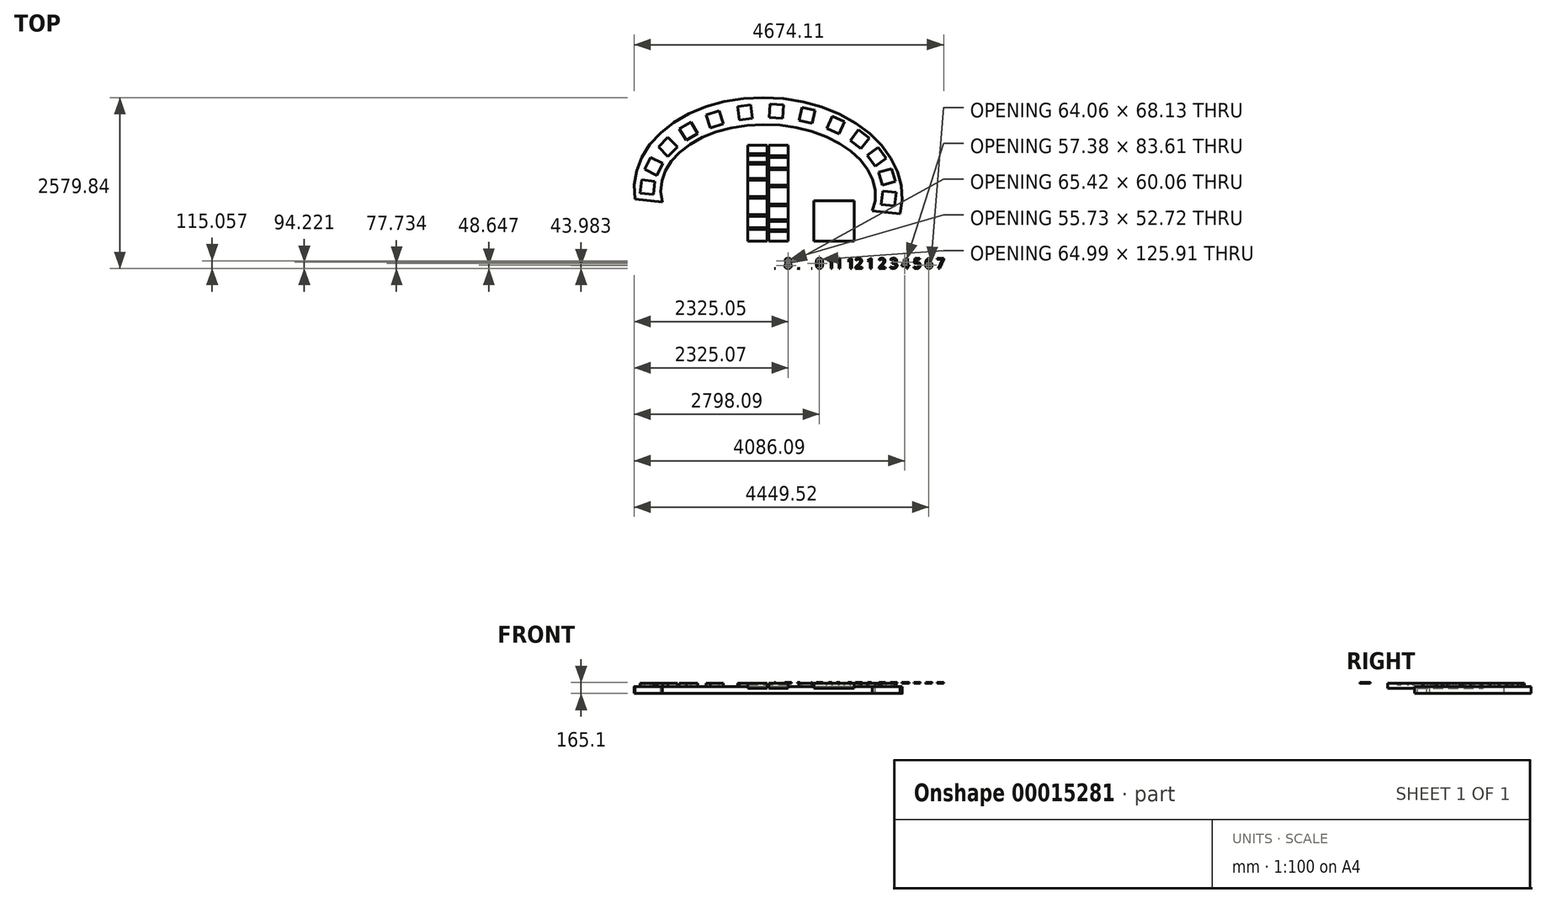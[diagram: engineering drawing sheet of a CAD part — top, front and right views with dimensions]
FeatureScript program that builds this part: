
annotation { "Feature Type Name" : "Feature", "Feature Type Description" : "" }
export const myFeature = defineFeature(function(context is Context, id is Id, definition is map)
    precondition{}
    {
        {
            var Q0;
            Q0=qCreatedBy(makeId("Top.planeOp"),FACE);
            var sketch = newSketch(context, id + "F0", { "sketchPlane" : qUnion([Q0])});
            skLineSegment(sketch, "E0", {"start": v(0, 0) * mm, "end": v(1346.2, 0) * mm, "construction": true});
            skLineSegment(sketch, "E1", {"start": v(0, 0) * mm, "end": v(-1346.2, 0) * mm, "construction": true});
            skLineSegment(sketch, "E2", {"start": v(0, 0) * mm, "end": v(0, 1231.9) * mm, "construction": true});
            skLineSegment(sketch, "E3", {"start": v(0, 0) * mm, "end": v(-1794.42, -235.08) * mm, "construction": true});
            skLineSegment(sketch, "E4", {"start": v(-1794.42, -235.08) * mm, "end": v(0, 1231.9) * mm, "construction": true});
            skLineSegment(sketch, "E5", {"start": v(0, 0) * mm, "end": v(-1820.55, 83.2) * mm, "construction": true});
            skLineSegment(sketch, "E6", {"start": v(-1820.55, 83.2) * mm, "end": v(0, 1231.9) * mm, "construction": true});
            skLineSegment(sketch, "E7", {"start": v(0, 0) * mm, "end": v(-1726.54, 397.25) * mm, "construction": true});
            skLineSegment(sketch, "E8", {"start": v(-1726.54, 397.25) * mm, "end": v(0, 1231.9) * mm, "construction": true});
            skLineSegment(sketch, "E9", {"start": v(0, 0) * mm, "end": v(-1513.04, 691.8) * mm, "construction": true});
            skLineSegment(sketch, "E10", {"start": v(-1513.04, 691.8) * mm, "end": v(0, 1231.9) * mm, "construction": true});
            skLineSegment(sketch, "E11", {"start": v(0, 0) * mm, "end": v(-1200.5, 928.47) * mm, "construction": true});
            skLineSegment(sketch, "E12", {"start": v(-1200.5, 928.47) * mm, "end": v(0, 1231.9) * mm, "construction": true});
            skLineSegment(sketch, "E13", {"start": v(-1346.2, 0) * mm, "end": v(-805.17, 1106.74) * mm, "construction": true});
            skLineSegment(sketch, "E14", {"start": v(-805.17, 1106.74) * mm, "end": v(1346.2, 0) * mm, "construction": true});
            skLineSegment(sketch, "E15", {"start": v(-1346.2, 0) * mm, "end": v(-348.76, 1210.44) * mm, "construction": true});
            skLineSegment(sketch, "E16", {"start": v(-348.76, 1210.44) * mm, "end": v(1346.2, 0) * mm, "construction": true});
            skLineSegment(sketch, "E17", {"start": v(-1346.2, 0) * mm, "end": v(124.87, 1230.26) * mm, "construction": true});
            skLineSegment(sketch, "E18", {"start": v(124.87, 1230.26) * mm, "end": v(1346.2, 0) * mm, "construction": true});
            skLineSegment(sketch, "E19", {"start": v(1346.2, 0) * mm, "end": v(589.88, 1167) * mm, "construction": true});
            skLineSegment(sketch, "E20", {"start": v(589.88, 1167) * mm, "end": v(-1346.2, 0) * mm, "construction": true});
            skLineSegment(sketch, "E21", {"start": v(1346.2, 0) * mm, "end": v(1020.46, 1022.52) * mm, "construction": true});
            skLineSegment(sketch, "E22", {"start": v(1020.46, 1022.52) * mm, "end": v(-1346.2, 0) * mm, "construction": true});
            skLineSegment(sketch, "E23", {"start": v(1346.2, 0) * mm, "end": v(1382.14, 805.65) * mm, "construction": true});
            skLineSegment(sketch, "E24", {"start": v(1382.14, 805.65) * mm, "end": v(-1346.2, 0) * mm, "construction": true});
            skLineSegment(sketch, "E25", {"start": v(0, 1231.9) * mm, "end": v(1639.4, 543.68) * mm, "construction": true});
            skLineSegment(sketch, "E26", {"start": v(1639.4, 543.68) * mm, "end": v(0, 0) * mm, "construction": true});
            skLineSegment(sketch, "E27", {"start": v(0, 0) * mm, "end": v(1794.05, 237.83) * mm, "construction": true});
            skLineSegment(sketch, "E28", {"start": v(1794.05, 237.83) * mm, "end": v(0, 1231.9) * mm, "construction": true});
            skLineSegment(sketch, "E29", {"start": v(0, 1231.9) * mm, "end": v(1820.38, -86.92) * mm, "construction": true});
            skLineSegment(sketch, "E30", {"start": v(1820.38, -86.92) * mm, "end": v(0, 0) * mm, "construction": true});
            skLineSegment(sketch, "E31", {"start": v(0, 0) * mm, "end": v(1726.06, -399.31) * mm, "construction": true});
            skLineSegment(sketch, "E32", {"start": v(1726.06, -399.31) * mm, "end": v(0, 1231.9) * mm, "construction": true});
            skPoint(sketch, "E33", {"position": v(-1794.42, -235.08) * mm});
            skPoint(sketch, "E34", {"position": v(-1820.55, 83.2) * mm});
            skPoint(sketch, "E35", {"position": v(-1726.54, 397.25) * mm});
            skPoint(sketch, "E36", {"position": v(-1513.04, 691.8) * mm});
            skPoint(sketch, "E37", {"position": v(-1200.5, 928.47) * mm});
            skPoint(sketch, "E38", {"position": v(-805.17, 1106.74) * mm});
            skPoint(sketch, "E39", {"position": v(-348.76, 1210.44) * mm});
            skPoint(sketch, "E40", {"position": v(124.87, 1230.26) * mm});
            skPoint(sketch, "E41", {"position": v(589.88, 1167) * mm});
            skPoint(sketch, "E42", {"position": v(1020.46, 1022.52) * mm});
            skPoint(sketch, "E43", {"position": v(1382.14, 805.65) * mm});
            skPoint(sketch, "E44", {"position": v(1639.4, 543.68) * mm});
            skPoint(sketch, "E45", {"position": v(1794.05, 237.83) * mm});
            skPoint(sketch, "E46", {"position": v(1820.38, -86.92) * mm});
            skPoint(sketch, "E47", {"position": v(0, 0) * mm});
            skPoint(sketch, "E48", {"position": v(0, 1231.9) * mm});
            skPoint(sketch, "E49", {"position": v(0, 717.55) * mm});
            skPoint(sketch, "E50", {"position": v(0, -730.25) * mm});
            skPoint(sketch, "E51", {"position": v(0, -571.5) * mm});
            skPoint(sketch, "E52", {"position": v(0, -419.1) * mm});
            skPoint(sketch, "E53", {"position": v(0, -184.15) * mm});
            skPoint(sketch, "E54", {"position": v(0, 101.6) * mm});
            skPoint(sketch, "E55", {"position": v(0, 361.95) * mm});
            skPoint(sketch, "E56", {"position": v(0, 546.1) * mm});
            skPoint(sketch, "E57", {"position": v(0, 577.85) * mm});
            skPoint(sketch, "E58", {"position": v(0, 444.5) * mm});
            skPoint(sketch, "E59", {"position": v(0, 203.2) * mm});
            skPoint(sketch, "E60", {"position": v(0, -69.85) * mm});
            skPoint(sketch, "E61", {"position": v(0, -342.9) * mm});
            skPoint(sketch, "E62", {"position": v(0, -539.75) * mm});
            skSolve(sketch);
        }
        {
            var Q0;
            Q0=qCreatedBy(makeId("Top.planeOp"),FACE);
            var sketch = newSketch(context, id + "F1", { "sketchPlane" : qUnion([Q0])});
            skPoint(sketch, "E63", {"position": v(-1794.42, -235.08) * mm});
            skPoint(sketch, "E64", {"position": v(-1820.55, 83.2) * mm});
            skPoint(sketch, "E65", {"position": v(-1726.54, 397.25) * mm});
            skPoint(sketch, "E66", {"position": v(-1513.04, 691.8) * mm});
            skPoint(sketch, "E67", {"position": v(-1200.5, 928.47) * mm});
            skPoint(sketch, "E68", {"position": v(-805.17, 1106.74) * mm});
            skPoint(sketch, "E69", {"position": v(-348.76, 1210.44) * mm});
            skPoint(sketch, "E70", {"position": v(0, 1231.9) * mm});
            skPoint(sketch, "E71", {"position": v(124.87, 1230.26) * mm});
            skPoint(sketch, "E72", {"position": v(589.88, 1167) * mm});
            skPoint(sketch, "E73", {"position": v(1020.46, 1022.52) * mm});
            skPoint(sketch, "E74", {"position": v(1382.14, 805.65) * mm});
            skPoint(sketch, "E75", {"position": v(1639.4, 543.68) * mm});
            skPoint(sketch, "E76", {"position": v(1794.05, 237.83) * mm});
            skPoint(sketch, "E77", {"position": v(1820.38, -86.92) * mm});
            skPoint(sketch, "E78", {"position": v(1726.06, -399.31) * mm});
            skPoint(sketch, "E79", {"position": v(0, 717.55) * mm});
            skPoint(sketch, "E80", {"position": v(0, 546.1) * mm});
            skPoint(sketch, "E81", {"position": v(0, 361.95) * mm});
            skPoint(sketch, "E82", {"position": v(0, 101.6) * mm});
            skPoint(sketch, "E83", {"position": v(0, -184.15) * mm});
            skPoint(sketch, "E84", {"position": v(0, -419.1) * mm});
            skPoint(sketch, "E85", {"position": v(0, -571.5) * mm});
            skPoint(sketch, "E86", {"position": v(0, -730.25) * mm});
            skLineSegment(sketch, "E87", {"start": v(304.8, 717.55) * mm, "end": v(-304.8, 717.55) * mm});
            skLineSegment(sketch, "E88", {"start": v(0, 546.1) * mm, "end": v(304.8, 546.1) * mm, "construction": true});
            skLineSegment(sketch, "E89", {"start": v(0, 361.95) * mm, "end": v(304.8, 361.95) * mm, "construction": true});
            skLineSegment(sketch, "E90", {"start": v(0, 101.6) * mm, "end": v(304.8, 101.6) * mm, "construction": true});
            skLineSegment(sketch, "E91", {"start": v(0, -184.15) * mm, "end": v(304.8, -184.15) * mm, "construction": true});
            skLineSegment(sketch, "E92", {"start": v(0, -419.1) * mm, "end": v(304.8, -419.1) * mm, "construction": true});
            skLineSegment(sketch, "E93", {"start": v(0, -571.5) * mm, "end": v(304.8, -571.5) * mm, "construction": true});
            skLineSegment(sketch, "E94", {"start": v(-304.8, -730.25) * mm, "end": v(304.8, -730.25) * mm});
            skPoint(sketch, "E95", {"position": v(0, -539.75) * mm});
            skPoint(sketch, "E96", {"position": v(0, -342.9) * mm});
            skPoint(sketch, "E97", {"position": v(0, 203.2) * mm});
            skPoint(sketch, "E98", {"position": v(0, 444.5) * mm});
            skPoint(sketch, "E99", {"position": v(0, 577.85) * mm});
            skPoint(sketch, "E100", {"position": v(0, -69.85) * mm});
            skLineSegment(sketch, "E101", {"start": v(0, -539.75) * mm, "end": v(-304.8, -539.75) * mm, "construction": true});
            skLineSegment(sketch, "E102", {"start": v(0, -342.9) * mm, "end": v(-304.8, -342.9) * mm, "construction": true});
            skLineSegment(sketch, "E103", {"start": v(0, -69.85) * mm, "end": v(-304.8, -69.85) * mm, "construction": true});
            skLineSegment(sketch, "E104", {"start": v(0, 203.2) * mm, "end": v(-304.8, 203.2) * mm, "construction": true});
            skLineSegment(sketch, "E105", {"start": v(0, 444.5) * mm, "end": v(-304.8, 444.5) * mm, "construction": true});
            skLineSegment(sketch, "E106", {"start": v(0, 577.85) * mm, "end": v(-304.8, 577.85) * mm, "construction": true});
            skPoint(sketch, "E107", {"position": v(304.8, -730.25) * mm});
            skPoint(sketch, "E108", {"position": v(-304.8, -730.25) * mm});
            skLineSegment(sketch, "E109", {"start": v(304.8, -730.25) * mm, "end": v(304.8, 717.55) * mm});
            skLineSegment(sketch, "E110", {"start": v(-304.8, -730.25) * mm, "end": v(-304.8, 717.55) * mm});
            skLineSegment(sketch, "E111", {"start": v(0, 717.55) * mm, "end": v(0, -730.25) * mm, "construction": true});
            skLineSegment(sketch, "E112", {"start": v(-1794.42, -235.08) * mm, "end": v(-1726.54, 397.25) * mm, "construction": true});
            skLineSegment(sketch, "E113", {"start": v(-1820.55, 83.2) * mm, "end": v(-1513.04, 691.8) * mm, "construction": true});
            skLineSegment(sketch, "E114", {"start": v(-1726.54, 397.25) * mm, "end": v(-1200.5, 928.47) * mm, "construction": true});
            skLineSegment(sketch, "E115", {"start": v(-1513.04, 691.8) * mm, "end": v(-805.17, 1106.74) * mm, "construction": true});
            skLineSegment(sketch, "E116", {"start": v(-1200.5, 928.47) * mm, "end": v(-348.76, 1210.44) * mm, "construction": true});
            skLineSegment(sketch, "E117", {"start": v(-805.17, 1106.74) * mm, "end": v(124.87, 1230.26) * mm, "construction": true});
            skLineSegment(sketch, "E118", {"start": v(-348.76, 1210.44) * mm, "end": v(589.88, 1167) * mm, "construction": true});
            skLineSegment(sketch, "E119", {"start": v(124.87, 1230.26) * mm, "end": v(1020.46, 1022.52) * mm, "construction": true});
            skLineSegment(sketch, "E120", {"start": v(589.88, 1167) * mm, "end": v(1382.14, 805.65) * mm, "construction": true});
            skLineSegment(sketch, "E121", {"start": v(1020.46, 1022.52) * mm, "end": v(1639.4, 543.68) * mm, "construction": true});
            skLineSegment(sketch, "E122", {"start": v(1382.14, 805.65) * mm, "end": v(1794.05, 237.83) * mm, "construction": true});
            skLineSegment(sketch, "E123", {"start": v(1639.4, 543.68) * mm, "end": v(1820.38, -86.92) * mm, "construction": true});
            skLineSegment(sketch, "E124", {"start": v(1794.05, 237.83) * mm, "end": v(1726.06, -399.31) * mm, "construction": true});
            skCircle(sketch, "E125.cCircle", {"center": v(-1820.55, 83.2) * mm, "radius": 101.6 * mm, "construction": true});
            skLineSegment(sketch, "E125.0", {"start": v(-1932.41, -6.97) * mm, "end": v(-1910.73, 195.07) * mm});
            skLineSegment(sketch, "E125.1", {"start": v(-1910.73, 195.07) * mm, "end": v(-1708.69, 173.38) * mm});
            skLineSegment(sketch, "E125.2", {"start": v(-1708.69, 173.38) * mm, "end": v(-1730.37, -28.66) * mm});
            skLineSegment(sketch, "E125.3", {"start": v(-1730.37, -28.66) * mm, "end": v(-1932.41, -6.97) * mm});
            skPoint(sketch, "E125.0.midPoint", {"position": v(-1921.57, 94.05) * mm});
            skCircle(sketch, "E126.cCircle", {"center": v(-1726.54, 397.25) * mm, "radius": 101.6 * mm, "construction": true});
            skLineSegment(sketch, "E126.0", {"start": v(-1681.68, 260.75) * mm, "end": v(-1863.04, 352.39) * mm});
            skLineSegment(sketch, "E126.1", {"start": v(-1863.04, 352.39) * mm, "end": v(-1771.4, 533.75) * mm});
            skLineSegment(sketch, "E126.2", {"start": v(-1771.4, 533.75) * mm, "end": v(-1590.04, 442.11) * mm});
            skLineSegment(sketch, "E126.3", {"start": v(-1590.04, 442.11) * mm, "end": v(-1681.68, 260.75) * mm});
            skPoint(sketch, "E126.0.midPoint", {"position": v(-1772.36, 306.57) * mm});
            skCircle(sketch, "E127.cCircle", {"center": v(-1513.04, 691.8) * mm, "radius": 101.6 * mm, "construction": true});
            skLineSegment(sketch, "E127.0", {"start": v(-1512.34, 548.12) * mm, "end": v(-1656.73, 691.1) * mm});
            skLineSegment(sketch, "E127.1", {"start": v(-1656.73, 691.1) * mm, "end": v(-1513.75, 835.49) * mm});
            skLineSegment(sketch, "E127.2", {"start": v(-1513.75, 835.49) * mm, "end": v(-1369.36, 692.51) * mm});
            skLineSegment(sketch, "E127.3", {"start": v(-1369.36, 692.51) * mm, "end": v(-1512.34, 548.12) * mm});
            skPoint(sketch, "E127.0.midPoint", {"position": v(-1584.53, 619.61) * mm});
            skCircle(sketch, "E128.cCircle", {"center": v(-1200.5, 928.47) * mm, "radius": 101.6 * mm, "construction": true});
            skLineSegment(sketch, "E128.0", {"start": v(-1236.77, 789.44) * mm, "end": v(-1339.53, 964.75) * mm});
            skLineSegment(sketch, "E128.1", {"start": v(-1339.53, 964.75) * mm, "end": v(-1164.22, 1067.5) * mm});
            skLineSegment(sketch, "E128.2", {"start": v(-1164.22, 1067.5) * mm, "end": v(-1061.47, 892.2) * mm});
            skLineSegment(sketch, "E128.3", {"start": v(-1061.47, 892.2) * mm, "end": v(-1236.77, 789.44) * mm});
            skPoint(sketch, "E128.0.midPoint", {"position": v(-1288.15, 877.1) * mm});
            skCircle(sketch, "E129.cCircle", {"center": v(-805.17, 1106.74) * mm, "radius": 101.6 * mm, "construction": true});
            skLineSegment(sketch, "E129.0", {"start": v(-869.7, 978.35) * mm, "end": v(-933.55, 1171.26) * mm});
            skLineSegment(sketch, "E129.1", {"start": v(-933.55, 1171.26) * mm, "end": v(-740.65, 1235.12) * mm});
            skLineSegment(sketch, "E129.2", {"start": v(-740.65, 1235.12) * mm, "end": v(-676.79, 1042.21) * mm});
            skLineSegment(sketch, "E129.3", {"start": v(-676.79, 1042.21) * mm, "end": v(-869.7, 978.35) * mm});
            skPoint(sketch, "E129.0.midPoint", {"position": v(-901.62, 1074.8) * mm});
            skCircle(sketch, "E130.cCircle", {"center": v(-348.76, 1210.44) * mm, "radius": 101.6 * mm, "construction": true});
            skLineSegment(sketch, "E130.0", {"start": v(-436.1, 1096.34) * mm, "end": v(-462.86, 1297.77) * mm});
            skLineSegment(sketch, "E130.1", {"start": v(-462.86, 1297.77) * mm, "end": v(-261.42, 1324.53) * mm});
            skLineSegment(sketch, "E130.2", {"start": v(-261.42, 1324.53) * mm, "end": v(-234.67, 1123.1) * mm});
            skLineSegment(sketch, "E130.3", {"start": v(-234.67, 1123.1) * mm, "end": v(-436.1, 1096.34) * mm});
            skPoint(sketch, "E130.0.midPoint", {"position": v(-449.48, 1197.06) * mm});
            skCircle(sketch, "E131.cCircle", {"center": v(124.87, 1230.26) * mm, "radius": 101.6 * mm, "construction": true});
            skLineSegment(sketch, "E131.0", {"start": v(231.05, 1327.05) * mm, "end": v(221.66, 1124.07) * mm});
            skLineSegment(sketch, "E131.1", {"start": v(221.66, 1124.07) * mm, "end": v(18.68, 1133.46) * mm});
            skLineSegment(sketch, "E131.2", {"start": v(18.68, 1133.46) * mm, "end": v(28.07, 1336.45) * mm});
            skLineSegment(sketch, "E131.3", {"start": v(28.07, 1336.45) * mm, "end": v(231.05, 1327.05) * mm});
            skPoint(sketch, "E131.0.midPoint", {"position": v(226.36, 1225.56) * mm});
            skCircle(sketch, "E132.cCircle", {"center": v(589.88, 1167) * mm, "radius": 101.6 * mm, "construction": true});
            skLineSegment(sketch, "E132.0", {"start": v(665.9, 1045.07) * mm, "end": v(467.95, 1090.99) * mm});
            skLineSegment(sketch, "E132.1", {"start": v(467.95, 1090.99) * mm, "end": v(513.87, 1288.93) * mm});
            skLineSegment(sketch, "E132.2", {"start": v(513.87, 1288.93) * mm, "end": v(711.81, 1243.02) * mm});
            skLineSegment(sketch, "E132.3", {"start": v(711.81, 1243.02) * mm, "end": v(665.9, 1045.07) * mm});
            skPoint(sketch, "E132.0.midPoint", {"position": v(566.93, 1068.03) * mm});
            skCircle(sketch, "E133.cCircle", {"center": v(1020.46, 1022.52) * mm, "radius": 101.6 * mm, "construction": true});
            skLineSegment(sketch, "E133.0", {"start": v(1155.06, 1072.8) * mm, "end": v(1070.73, 887.92) * mm});
            skLineSegment(sketch, "E133.1", {"start": v(1070.73, 887.92) * mm, "end": v(885.85, 972.24) * mm});
            skLineSegment(sketch, "E133.2", {"start": v(885.85, 972.24) * mm, "end": v(970.18, 1157.12) * mm});
            skLineSegment(sketch, "E133.3", {"start": v(970.18, 1157.12) * mm, "end": v(1155.06, 1072.8) * mm});
            skPoint(sketch, "E133.0.midPoint", {"position": v(1112.9, 980.36) * mm});
            skCircle(sketch, "E134.cCircle", {"center": v(1382.14, 805.65) * mm, "radius": 101.6 * mm, "construction": true});
            skLineSegment(sketch, "E134.0", {"start": v(1524.66, 823.84) * mm, "end": v(1400.33, 663.12) * mm});
            skLineSegment(sketch, "E134.1", {"start": v(1400.33, 663.12) * mm, "end": v(1239.6, 787.46) * mm});
            skLineSegment(sketch, "E134.2", {"start": v(1239.6, 787.46) * mm, "end": v(1363.95, 948.18) * mm});
            skLineSegment(sketch, "E134.3", {"start": v(1363.95, 948.18) * mm, "end": v(1524.66, 823.84) * mm});
            skPoint(sketch, "E134.0.midPoint", {"position": v(1462.5, 743.48) * mm});
            skCircle(sketch, "E135.cCircle", {"center": v(1639.4, 543.68) * mm, "radius": 101.6 * mm, "construction": true});
            skLineSegment(sketch, "E135.0", {"start": v(1616.82, 401.78) * mm, "end": v(1497.5, 566.26) * mm});
            skLineSegment(sketch, "E135.1", {"start": v(1497.5, 566.26) * mm, "end": v(1661.98, 685.58) * mm});
            skLineSegment(sketch, "E135.2", {"start": v(1661.98, 685.58) * mm, "end": v(1781.3, 521.1) * mm});
            skLineSegment(sketch, "E135.3", {"start": v(1781.3, 521.1) * mm, "end": v(1616.82, 401.78) * mm});
            skPoint(sketch, "E135.0.midPoint", {"position": v(1557.16, 484.02) * mm});
            skCircle(sketch, "E136.cCircle", {"center": v(1794.05, 237.83) * mm, "radius": 101.6 * mm, "construction": true});
            skLineSegment(sketch, "E136.0", {"start": v(1919.74, 168.2) * mm, "end": v(1724.42, 112.15) * mm});
            skLineSegment(sketch, "E136.1", {"start": v(1724.42, 112.15) * mm, "end": v(1668.37, 307.46) * mm});
            skLineSegment(sketch, "E136.2", {"start": v(1668.37, 307.46) * mm, "end": v(1863.69, 363.52) * mm});
            skLineSegment(sketch, "E136.3", {"start": v(1863.69, 363.52) * mm, "end": v(1919.74, 168.2) * mm});
            skPoint(sketch, "E136.0.midPoint", {"position": v(1822.08, 140.17) * mm});
            skCircle(sketch, "E137.cCircle", {"center": v(1820.38, -86.92) * mm, "radius": 101.6 * mm, "construction": true});
            skLineSegment(sketch, "E137.0", {"start": v(1910.62, -198.73) * mm, "end": v(1708.57, -177.17) * mm});
            skLineSegment(sketch, "E137.1", {"start": v(1708.57, -177.17) * mm, "end": v(1730.13, 24.89) * mm});
            skLineSegment(sketch, "E137.2", {"start": v(1730.13, 24.89) * mm, "end": v(1932.18, 3.33) * mm});
            skLineSegment(sketch, "E137.3", {"start": v(1932.18, 3.33) * mm, "end": v(1910.62, -198.73) * mm});
            skPoint(sketch, "E137.0.midPoint", {"position": v(1809.6, -187.95) * mm});
            skLineSegment(sketch, "E138.rect.bottom", {"start": v(12.7, -730.25) * mm, "end": v(-12.7, -730.25) * mm});
            skLineSegment(sketch, "E138.rect.left", {"start": v(12.7, -730.25) * mm, "end": v(12.7, 717.55) * mm});
            skLineSegment(sketch, "E138.rect.right", {"start": v(-12.7, -730.25) * mm, "end": v(-12.7, 717.55) * mm});
            skPoint(sketch, "E138.rect.middle", {"position": v(0, 0) * mm});
            skLineSegment(sketch, "E139.bottom", {"start": v(304.8, -584.2) * mm, "end": v(12.7, -584.2) * mm});
            skLineSegment(sketch, "E139.top", {"start": v(304.8, -558.8) * mm, "end": v(12.7, -558.8) * mm});
            skLineSegment(sketch, "E139.left", {"start": v(304.8, -584.2) * mm, "end": v(304.8, -558.8) * mm});
            skLineSegment(sketch, "E139.right", {"start": v(12.7, -584.2) * mm, "end": v(12.7, -558.8) * mm});
            skLineSegment(sketch, "E140.bottom", {"start": v(304.8, -431.8) * mm, "end": v(12.7, -431.8) * mm});
            skLineSegment(sketch, "E140.top", {"start": v(304.8, -406.4) * mm, "end": v(12.7, -406.4) * mm});
            skLineSegment(sketch, "E140.left", {"start": v(304.8, -431.8) * mm, "end": v(304.8, -406.4) * mm});
            skLineSegment(sketch, "E140.right", {"start": v(12.7, -431.8) * mm, "end": v(12.7, -406.4) * mm});
            skLineSegment(sketch, "E141.bottom", {"start": v(304.8, -196.85) * mm, "end": v(12.7, -196.85) * mm});
            skLineSegment(sketch, "E141.top", {"start": v(304.8, -171.45) * mm, "end": v(12.7, -171.45) * mm});
            skLineSegment(sketch, "E141.left", {"start": v(304.8, -196.85) * mm, "end": v(304.8, -171.45) * mm});
            skLineSegment(sketch, "E141.right", {"start": v(12.7, -196.85) * mm, "end": v(12.7, -171.45) * mm});
            skLineSegment(sketch, "E142.bottom", {"start": v(304.8, 88.9) * mm, "end": v(12.7, 88.9) * mm});
            skLineSegment(sketch, "E142.top", {"start": v(304.8, 114.3) * mm, "end": v(12.7, 114.3) * mm});
            skLineSegment(sketch, "E142.left", {"start": v(304.8, 88.9) * mm, "end": v(304.8, 114.3) * mm});
            skLineSegment(sketch, "E142.right", {"start": v(12.7, 88.9) * mm, "end": v(12.7, 114.3) * mm});
            skLineSegment(sketch, "E143.bottom", {"start": v(304.8, 349.25) * mm, "end": v(12.7, 349.25) * mm});
            skLineSegment(sketch, "E143.top", {"start": v(304.8, 374.65) * mm, "end": v(12.7, 374.65) * mm});
            skLineSegment(sketch, "E143.left", {"start": v(304.8, 349.25) * mm, "end": v(304.8, 374.65) * mm});
            skLineSegment(sketch, "E143.right", {"start": v(12.7, 349.25) * mm, "end": v(12.7, 374.65) * mm});
            skLineSegment(sketch, "E144.bottom", {"start": v(304.8, 533.4) * mm, "end": v(12.7, 533.4) * mm});
            skLineSegment(sketch, "E144.top", {"start": v(304.8, 558.8) * mm, "end": v(12.7, 558.8) * mm});
            skLineSegment(sketch, "E144.left", {"start": v(304.8, 533.4) * mm, "end": v(304.8, 558.8) * mm});
            skLineSegment(sketch, "E144.right", {"start": v(12.7, 533.4) * mm, "end": v(12.7, 558.8) * mm});
            skLineSegment(sketch, "E145.bottom", {"start": v(-304.8, 565.15) * mm, "end": v(-12.7, 565.15) * mm});
            skLineSegment(sketch, "E145.top", {"start": v(-304.8, 590.55) * mm, "end": v(-12.7, 590.55) * mm});
            skLineSegment(sketch, "E145.left", {"start": v(-304.8, 565.15) * mm, "end": v(-304.8, 590.55) * mm});
            skLineSegment(sketch, "E145.right", {"start": v(-12.7, 565.15) * mm, "end": v(-12.7, 590.55) * mm});
            skLineSegment(sketch, "E146.bottom", {"start": v(-304.8, 431.8) * mm, "end": v(-12.7, 431.8) * mm});
            skLineSegment(sketch, "E146.top", {"start": v(-304.8, 457.2) * mm, "end": v(-12.7, 457.2) * mm});
            skLineSegment(sketch, "E146.left", {"start": v(-304.8, 431.8) * mm, "end": v(-304.8, 457.2) * mm});
            skLineSegment(sketch, "E146.right", {"start": v(-12.7, 431.8) * mm, "end": v(-12.7, 457.2) * mm});
            skLineSegment(sketch, "E147.bottom", {"start": v(-304.8, 190.5) * mm, "end": v(-12.7, 190.5) * mm});
            skLineSegment(sketch, "E147.top", {"start": v(-304.8, 215.9) * mm, "end": v(-12.7, 215.9) * mm});
            skLineSegment(sketch, "E147.left", {"start": v(-304.8, 190.5) * mm, "end": v(-304.8, 215.9) * mm});
            skLineSegment(sketch, "E147.right", {"start": v(-12.7, 190.5) * mm, "end": v(-12.7, 215.9) * mm});
            skLineSegment(sketch, "E148.bottom", {"start": v(-304.8, -82.55) * mm, "end": v(-12.7, -82.55) * mm});
            skLineSegment(sketch, "E148.top", {"start": v(-304.8, -57.15) * mm, "end": v(-12.7, -57.15) * mm});
            skLineSegment(sketch, "E148.left", {"start": v(-304.8, -82.55) * mm, "end": v(-304.8, -57.15) * mm});
            skLineSegment(sketch, "E148.right", {"start": v(-12.7, -82.55) * mm, "end": v(-12.7, -57.15) * mm});
            skLineSegment(sketch, "E149.bottom", {"start": v(-304.8, -355.6) * mm, "end": v(-12.7, -355.6) * mm});
            skLineSegment(sketch, "E149.top", {"start": v(-304.8, -330.2) * mm, "end": v(-12.7, -330.2) * mm});
            skLineSegment(sketch, "E149.left", {"start": v(-304.8, -355.6) * mm, "end": v(-304.8, -330.2) * mm});
            skLineSegment(sketch, "E149.right", {"start": v(-12.7, -355.6) * mm, "end": v(-12.7, -330.2) * mm});
            skLineSegment(sketch, "E150.bottom", {"start": v(-304.8, -552.45) * mm, "end": v(-12.7, -552.45) * mm});
            skLineSegment(sketch, "E150.top", {"start": v(-304.8, -527.05) * mm, "end": v(-12.7, -527.05) * mm});
            skLineSegment(sketch, "E150.left", {"start": v(-304.8, -552.45) * mm, "end": v(-304.8, -527.05) * mm});
            skLineSegment(sketch, "E150.right", {"start": v(-12.7, -552.45) * mm, "end": v(-12.7, -527.05) * mm});
            skText(sketch, "E151", { "text": "7 8 9 10 11 12 1 2 3 4 5 6 7", "fontName": "OpenSans-Regular.ttf"});
            skLineSegment(sketch, "E152.bottom", {"start": v(65.3, -989.14) * mm, "end": v(211.64, -989.14) * mm});
            skLineSegment(sketch, "E152.top", {"start": v(65.3, -1141.54) * mm, "end": v(211.64, -1141.54) * mm});
            skLineSegment(sketch, "E152.left", {"start": v(65.3, -989.14) * mm, "end": v(65.3, -1141.54) * mm});
            skLineSegment(sketch, "E152.right", {"start": v(211.64, -989.14) * mm, "end": v(211.64, -1141.54) * mm});
            skLineSegment(sketch, "E153.bottom", {"start": v(211.64, -1141.54) * mm, "end": v(385.48, -1141.54) * mm});
            skLineSegment(sketch, "E153.top", {"start": v(211.64, -989.14) * mm, "end": v(385.48, -989.14) * mm});
            skLineSegment(sketch, "E153.left", {"start": v(211.64, -1141.54) * mm, "end": v(211.64, -989.14) * mm});
            skLineSegment(sketch, "E153.right", {"start": v(385.48, -1141.54) * mm, "end": v(385.48, -989.14) * mm});
            skLineSegment(sketch, "E154.bottom", {"start": v(385.48, -1141.54) * mm, "end": v(572.47, -1141.54) * mm});
            skLineSegment(sketch, "E154.top", {"start": v(385.48, -989.14) * mm, "end": v(572.47, -989.14) * mm});
            skLineSegment(sketch, "E154.right", {"start": v(572.47, -1141.54) * mm, "end": v(572.47, -989.14) * mm});
            skLineSegment(sketch, "E155.bottom", {"start": v(572.47, -989.14) * mm, "end": v(870.26, -989.14) * mm});
            skLineSegment(sketch, "E155.top", {"start": v(572.47, -1141.54) * mm, "end": v(870.26, -1141.54) * mm});
            skLineSegment(sketch, "E155.left", {"start": v(572.47, -989.14) * mm, "end": v(572.47, -1141.54) * mm});
            skLineSegment(sketch, "E155.right", {"start": v(870.26, -989.14) * mm, "end": v(870.26, -1141.54) * mm});
            skLineSegment(sketch, "E156", {"start": v(-2863.58, 0) * mm, "end": v(3232.42, -6.97) * mm, "construction": true});
            skLineSegment(sketch, "E157", {"start": v(0, 2273.5) * mm, "end": v(0, -2824.57) * mm, "construction": true});
            skPoint(sketch, "E158", {"position": v(0, 1435.1) * mm});
            skPoint(sketch, "E159", {"position": v(0, 1028.7) * mm});
            skPoint(sketch, "E160", {"position": v(1619.22, -58.91) * mm});
            skPoint(sketch, "E161", {"position": v(2021.73, -113.73) * mm});
            skEllipticalArc(sketch, "E162", {});
            skLineSegment(sketch, "E163", {"start": v(-2012.12, -94.57) * mm, "end": v(-1596.35, -139.2) * mm});
            skLineSegment(sketch, "E164", {"start": v(1574.18, -276.25) * mm, "end": v(1988.6, -320.47) * mm});
            skEllipticalArc(sketch, "E165.trimOffspring", {});
            const initialGuessF1  = {"E151": [0.0653, -1.14154, 1, 0, 0.1524], "E162": [0, 0, 0.9984214700477535, -0.05616554235189876, 2.0249262350496036, 1.4339711488939468, 6.137427259642238, 3.286760696660397], "E165.trimOffspring": [0, 0, 0.9993387333177954, -0.03636063930659239, 1.6202917132659667, 1.0282937856299592, 6.068741439196701, 3.334519765623312]};
            skSetInitialGuess(sketch, initialGuessF1);
            skSolve(sketch);
        }
        {
            var Q0;
            Q0=makeQuery(id+"F1.imprint","IMPRINT",FACE,{"disambiguationData":[TD([[makeQuery(id+"F1.imprint","IMPRINT",EDGE,{"derivedFrom":sQuery(id+"F1.wireOp",EDGE,"E135.0")}),-1.0]])]});
            var Q1;
            Q1=makeQuery(id+"F1.imprint","IMPRINT",FACE,{"disambiguationData":[TD([[makeQuery(id+"F1.imprint","IMPRINT",EDGE,{"derivedFrom":sQuery(id+"F1.wireOp",EDGE,"E134.0")}),-1.0]])]});
            var Q2;
            Q2=makeQuery(id+"F1.imprint","IMPRINT",FACE,{"disambiguationData":[TD([[makeQuery(id+"F1.imprint","IMPRINT",EDGE,{"derivedFrom":sQuery(id+"F1.wireOp",EDGE,"E133.0")}),-1.0]])]});
            var Q3;
            Q3=makeQuery(id+"F1.imprint","IMPRINT",FACE,{"disambiguationData":[TD([[makeQuery(id+"F1.imprint","IMPRINT",EDGE,{"derivedFrom":sQuery(id+"F1.wireOp",EDGE,"E132.0")}),-1.0]])]});
            var Q4;
            Q4=makeQuery(id+"F1.imprint","IMPRINT",FACE,{"disambiguationData":[TD([[makeQuery(id+"F1.imprint","IMPRINT",EDGE,{"derivedFrom":sQuery(id+"F1.wireOp",EDGE,"E131.0")}),-1.0]])]});
            var Q5;
            Q5=makeQuery(id+"F1.imprint","IMPRINT",FACE,{"disambiguationData":[TD([[makeQuery(id+"F1.imprint","IMPRINT",EDGE,{"derivedFrom":sQuery(id+"F1.wireOp",EDGE,"E130.0")}),-1.0]])]});
            var Q6;
            Q6=makeQuery(id+"F1.imprint","IMPRINT",FACE,{"disambiguationData":[TD([[makeQuery(id+"F1.imprint","IMPRINT",EDGE,{"derivedFrom":sQuery(id+"F1.wireOp",EDGE,"E129.0")}),-1.0]])]});
            var Q7;
            Q7=makeQuery(id+"F1.imprint","IMPRINT",FACE,{"disambiguationData":[TD([[makeQuery(id+"F1.imprint","IMPRINT",EDGE,{"derivedFrom":sQuery(id+"F1.wireOp",EDGE,"E128.0")}),-1.0]])]});
            var Q8;
            Q8=makeQuery(id+"F1.imprint","IMPRINT",FACE,{"disambiguationData":[TD([[makeQuery(id+"F1.imprint","IMPRINT",EDGE,{"derivedFrom":sQuery(id+"F1.wireOp",EDGE,"E127.0")}),-1.0]])]});
            var Q9;
            Q9=makeQuery(id+"F1.imprint","IMPRINT",FACE,{"disambiguationData":[TD([[makeQuery(id+"F1.imprint","IMPRINT",EDGE,{"derivedFrom":sQuery(id+"F1.wireOp",EDGE,"E126.0")}),-1.0]])]});
            var Q10;
            Q10=makeQuery(id+"F1.imprint","IMPRINT",FACE,{"disambiguationData":[TD([[makeQuery(id+"F1.imprint","IMPRINT",EDGE,{"derivedFrom":sQuery(id+"F1.wireOp",EDGE,"E125.0")}),-1.0]])]});
            var Q11;
            Q11=makeQuery(id+"F1.imprint","IMPRINT",FACE,{"disambiguationData":[TD([[makeQuery(id+"F1.imprint","IMPRINT",EDGE,{"derivedFrom":sQuery(id+"F1.wireOp",EDGE,"E137.0")}),-1.0]])]});
            var Q12;
            Q12=makeQuery(id+"F1.imprint","IMPRINT",FACE,{"disambiguationData":[TD([[makeQuery(id+"F1.imprint","IMPRINT",EDGE,{"derivedFrom":sQuery(id+"F1.wireOp",EDGE,"E136.0")}),-1.0]])]});
            extrude(context, id + "F2", {"entities" : qUnion([Q0, Q1, Q2, Q3, Q4, Q5, Q6, Q7, Q8, Q9, Q10, Q11, Q12]), "oppositeDirection" : true, "depth" : 50.8 * mm});
        }
        {
            var Q0;
            {var subQ1=sQuery(id+"F1.wireOp",EDGE,"E149.bottom");Q0=makeQuery(id+"F1.imprint","IMPRINT",FACE,{"disambiguationData":[TD([[makeQuery(id+"F1.imprint","IMPRINT",EDGE,{"derivedFrom":subQ1}),-1.0]])]});}
            var Q1;
            {var subQ1=sQuery(id+"F1.wireOp",EDGE,"E148.bottom");Q1=makeQuery(id+"F1.imprint","IMPRINT",FACE,{"disambiguationData":[TD([[makeQuery(id+"F1.imprint","IMPRINT",EDGE,{"derivedFrom":subQ1}),-1.0]])]});}
            var Q2;
            {var subQ0=sQuery(id+"F1.wireOp",EDGE,"E139.bottom");Q2=makeQuery(id+"F1.imprint","IMPRINT",FACE,{"disambiguationData":[TD([[makeQuery(id+"F1.imprint","IMPRINT",EDGE,{"derivedFrom":subQ0}),1.0]])]});}
            var Q3;
            {var subQ0=sQuery(id+"F1.wireOp",EDGE,"E150.bottom");Q3=makeQuery(id+"F1.imprint","IMPRINT",FACE,{"disambiguationData":[TD([[makeQuery(id+"F1.imprint","IMPRINT",EDGE,{"derivedFrom":subQ0}),-1.0]])]});}
            var Q4;
            {var subQ0=sQuery(id+"F1.wireOp",EDGE,"E144.top");Q4=makeQuery(id+"F1.imprint","IMPRINT",FACE,{"disambiguationData":[TD([[makeQuery(id+"F1.imprint","IMPRINT",EDGE,{"derivedFrom":subQ0}),-1.0]])]});}
            var Q5;
            {var subQ0=sQuery(id+"F1.wireOp",EDGE,"E145.top");Q5=makeQuery(id+"F1.imprint","IMPRINT",FACE,{"disambiguationData":[TD([[makeQuery(id+"F1.imprint","IMPRINT",EDGE,{"derivedFrom":subQ0}),1.0]])]});}
            var Q6;
            {var subQ1=sQuery(id+"F1.wireOp",EDGE,"E143.top");Q6=makeQuery(id+"F1.imprint","IMPRINT",FACE,{"disambiguationData":[TD([[makeQuery(id+"F1.imprint","IMPRINT",EDGE,{"derivedFrom":subQ1}),-1.0]])]});}
            var Q7;
            {var subQ1=sQuery(id+"F1.wireOp",EDGE,"E147.bottom");Q7=makeQuery(id+"F1.imprint","IMPRINT",FACE,{"disambiguationData":[TD([[makeQuery(id+"F1.imprint","IMPRINT",EDGE,{"derivedFrom":subQ1}),-1.0]])]});}
            var Q8;
            {var subQ1=sQuery(id+"F1.wireOp",EDGE,"E145.bottom");Q8=makeQuery(id+"F1.imprint","IMPRINT",FACE,{"disambiguationData":[TD([[makeQuery(id+"F1.imprint","IMPRINT",EDGE,{"derivedFrom":subQ1}),-1.0]])]});}
            var Q9;
            {var subQ1=sQuery(id+"F1.wireOp",EDGE,"E139.top");Q9=makeQuery(id+"F1.imprint","IMPRINT",FACE,{"disambiguationData":[TD([[makeQuery(id+"F1.imprint","IMPRINT",EDGE,{"derivedFrom":subQ1}),-1.0]])]});}
            var Q10;
            {var subQ1=sQuery(id+"F1.wireOp",EDGE,"E146.bottom");Q10=makeQuery(id+"F1.imprint","IMPRINT",FACE,{"disambiguationData":[TD([[makeQuery(id+"F1.imprint","IMPRINT",EDGE,{"derivedFrom":subQ1}),-1.0]])]});}
            var Q11;
            {var subQ1=sQuery(id+"F1.wireOp",EDGE,"E141.top");Q11=makeQuery(id+"F1.imprint","IMPRINT",FACE,{"disambiguationData":[TD([[makeQuery(id+"F1.imprint","IMPRINT",EDGE,{"derivedFrom":subQ1}),-1.0]])]});}
            var Q12;
            {var subQ1=sQuery(id+"F1.wireOp",EDGE,"E142.top");Q12=makeQuery(id+"F1.imprint","IMPRINT",FACE,{"disambiguationData":[TD([[makeQuery(id+"F1.imprint","IMPRINT",EDGE,{"derivedFrom":subQ1}),-1.0]])]});}
            var Q13;
            {var subQ1=sQuery(id+"F1.wireOp",EDGE,"E140.top");Q13=makeQuery(id+"F1.imprint","IMPRINT",FACE,{"disambiguationData":[TD([[makeQuery(id+"F1.imprint","IMPRINT",EDGE,{"derivedFrom":subQ1}),-1.0]])]});}
            var Q14;
            Q14=makeQuery(id+"F1.imprint","IMPRINT",FACE,{"disambiguationData":[TD([[makeQuery(id+"F1.imprint","IMPRINT",EDGE,{"derivedFrom":sQuery(id+"F1.wireOp",EDGE,"E150.bottom")}),1.0]])]});
            var Q15;
            {var subQ9=sQuery(id+"F1.wireOp",EDGE,"E138.rect.bottom");Q15=makeQuery(id+"F1.imprint","IMPRINT",FACE,{"disambiguationData":[TD([[makeQuery(id+"F1.imprint","IMPRINT",EDGE,{"derivedFrom":subQ9}),-1.0]])]});}
            var Q16;
            Q16=makeQuery(id+"F1.imprint","IMPRINT",FACE,{"disambiguationData":[TD([[makeQuery(id+"F1.imprint","IMPRINT",EDGE,{"derivedFrom":sQuery(id+"F1.wireOp",EDGE,"E142.bottom")}),-1.0]])]});
            var Q17;
            Q17=makeQuery(id+"F1.imprint","IMPRINT",FACE,{"disambiguationData":[TD([[makeQuery(id+"F1.imprint","IMPRINT",EDGE,{"derivedFrom":sQuery(id+"F1.wireOp",EDGE,"E140.bottom")}),-1.0]])]});
            var Q18;
            Q18=makeQuery(id+"F1.imprint","IMPRINT",FACE,{"disambiguationData":[TD([[makeQuery(id+"F1.imprint","IMPRINT",EDGE,{"derivedFrom":sQuery(id+"F1.wireOp",EDGE,"E139.bottom")}),-1.0]])]});
            var Q19;
            Q19=makeQuery(id+"F1.imprint","IMPRINT",FACE,{"disambiguationData":[TD([[makeQuery(id+"F1.imprint","IMPRINT",EDGE,{"derivedFrom":sQuery(id+"F1.wireOp",EDGE,"E144.bottom")}),-1.0]])]});
            var Q20;
            Q20=makeQuery(id+"F1.imprint","IMPRINT",FACE,{"disambiguationData":[TD([[makeQuery(id+"F1.imprint","IMPRINT",EDGE,{"derivedFrom":sQuery(id+"F1.wireOp",EDGE,"E141.bottom")}),-1.0]])]});
            var Q21;
            Q21=makeQuery(id+"F1.imprint","IMPRINT",FACE,{"disambiguationData":[TD([[makeQuery(id+"F1.imprint","IMPRINT",EDGE,{"derivedFrom":sQuery(id+"F1.wireOp",EDGE,"E149.bottom")}),1.0]])]});
            var Q22;
            Q22=makeQuery(id+"F1.imprint","IMPRINT",FACE,{"disambiguationData":[TD([[makeQuery(id+"F1.imprint","IMPRINT",EDGE,{"derivedFrom":sQuery(id+"F1.wireOp",EDGE,"E147.bottom")}),1.0]])]});
            var Q23;
            Q23=makeQuery(id+"F1.imprint","IMPRINT",FACE,{"disambiguationData":[TD([[makeQuery(id+"F1.imprint","IMPRINT",EDGE,{"derivedFrom":sQuery(id+"F1.wireOp",EDGE,"E148.bottom")}),1.0]])]});
            var Q24;
            Q24=makeQuery(id+"F1.imprint","IMPRINT",FACE,{"disambiguationData":[TD([[makeQuery(id+"F1.imprint","IMPRINT",EDGE,{"derivedFrom":sQuery(id+"F1.wireOp",EDGE,"E146.bottom")}),1.0]])]});
            var Q25;
            Q25=makeQuery(id+"F1.imprint","IMPRINT",FACE,{"disambiguationData":[TD([[makeQuery(id+"F1.imprint","IMPRINT",EDGE,{"derivedFrom":sQuery(id+"F1.wireOp",EDGE,"E145.bottom")}),1.0]])]});
            var Q26;
            Q26=makeQuery(id+"F1.imprint","IMPRINT",FACE,{"disambiguationData":[TD([[makeQuery(id+"F1.imprint","IMPRINT",EDGE,{"derivedFrom":sQuery(id+"F1.wireOp",EDGE,"E143.bottom")}),-1.0]])]});
            extrude(context, id + "F3", {"entities" : qUnion([Q0, Q1, Q2, Q3, Q4, Q5, Q6, Q7, Q8, Q9, Q10, Q11, Q12, Q13, Q14, Q15, Q16, Q17, Q18, Q19, Q20, Q21, Q22, Q23, Q24, Q25, Q26]), "oppositeDirection" : true, "depth" : 76.2 * mm});
        }
        {
            var Q0;
            Q0=makeQuery(id+"F1.imprint","IMPRINT",FACE,{"disambiguationData":[TD([[makeQuery(id+"F1.imprint","IMPRINT",EDGE,{"derivedFrom":sQuery(id+"F1.wireOp",EDGE,"E139.bottom")}),-1.0]])]});
            var Q1;
            Q1=makeQuery(id+"F1.imprint","IMPRINT",FACE,{"disambiguationData":[TD([[makeQuery(id+"F1.imprint","IMPRINT",EDGE,{"derivedFrom":sQuery(id+"F1.wireOp",EDGE,"E150.bottom")}),1.0]])]});
            var Q2;
            Q2=makeQuery(id+"F1.imprint","IMPRINT",FACE,{"disambiguationData":[TD([[makeQuery(id+"F1.imprint","IMPRINT",EDGE,{"derivedFrom":sQuery(id+"F1.wireOp",EDGE,"E140.bottom")}),-1.0]])]});
            var Q3;
            Q3=makeQuery(id+"F1.imprint","IMPRINT",FACE,{"disambiguationData":[TD([[makeQuery(id+"F1.imprint","IMPRINT",EDGE,{"derivedFrom":sQuery(id+"F1.wireOp",EDGE,"E149.bottom")}),1.0]])]});
            var Q4;
            Q4=makeQuery(id+"F1.imprint","IMPRINT",FACE,{"disambiguationData":[TD([[makeQuery(id+"F1.imprint","IMPRINT",EDGE,{"derivedFrom":sQuery(id+"F1.wireOp",EDGE,"E141.bottom")}),-1.0]])]});
            var Q5;
            Q5=makeQuery(id+"F1.imprint","IMPRINT",FACE,{"disambiguationData":[TD([[makeQuery(id+"F1.imprint","IMPRINT",EDGE,{"derivedFrom":sQuery(id+"F1.wireOp",EDGE,"E148.bottom")}),1.0]])]});
            var Q6;
            Q6=makeQuery(id+"F1.imprint","IMPRINT",FACE,{"disambiguationData":[TD([[makeQuery(id+"F1.imprint","IMPRINT",EDGE,{"derivedFrom":sQuery(id+"F1.wireOp",EDGE,"E142.bottom")}),-1.0]])]});
            var Q7;
            Q7=makeQuery(id+"F1.imprint","IMPRINT",FACE,{"disambiguationData":[TD([[makeQuery(id+"F1.imprint","IMPRINT",EDGE,{"derivedFrom":sQuery(id+"F1.wireOp",EDGE,"E147.bottom")}),1.0]])]});
            var Q8;
            Q8=makeQuery(id+"F1.imprint","IMPRINT",FACE,{"disambiguationData":[TD([[makeQuery(id+"F1.imprint","IMPRINT",EDGE,{"derivedFrom":sQuery(id+"F1.wireOp",EDGE,"E143.bottom")}),-1.0]])]});
            var Q9;
            Q9=makeQuery(id+"F1.imprint","IMPRINT",FACE,{"disambiguationData":[TD([[makeQuery(id+"F1.imprint","IMPRINT",EDGE,{"derivedFrom":sQuery(id+"F1.wireOp",EDGE,"E146.bottom")}),1.0]])]});
            var Q10;
            Q10=makeQuery(id+"F1.imprint","IMPRINT",FACE,{"disambiguationData":[TD([[makeQuery(id+"F1.imprint","IMPRINT",EDGE,{"derivedFrom":sQuery(id+"F1.wireOp",EDGE,"E144.bottom")}),-1.0]])]});
            var Q11;
            Q11=makeQuery(id+"F1.imprint","IMPRINT",FACE,{"disambiguationData":[TD([[makeQuery(id+"F1.imprint","IMPRINT",EDGE,{"derivedFrom":sQuery(id+"F1.wireOp",EDGE,"E145.bottom")}),1.0]])]});
            var Q12;
            {var subQ9=sQuery(id+"F1.wireOp",EDGE,"E138.rect.bottom");Q12=makeQuery(id+"F1.imprint","IMPRINT",FACE,{"disambiguationData":[TD([[makeQuery(id+"F1.imprint","IMPRINT",EDGE,{"derivedFrom":subQ9}),-1.0]])]});}
            extrude(context, id + "F4", {"entities" : qUnion([Q0, Q1, Q2, Q3, Q4, Q5, Q6, Q7, Q8, Q9, Q10, Q11, Q12]), "operationType" : NewBodyOperationType.REMOVE, "oppositeDirection" : true, "depth" : 25.4 * mm});
        }
        {
            var Q0;
            {var subQ2=sQuery(id+"F1.wireOp",EDGE,"E151.sketch_text.stroke-0");Q0=makeQuery(id+"F1.imprint","IMPRINT",FACE,{"disambiguationData":[TD([[makeQuery(id+"F1.imprint","IMPRINT",EDGE,{"derivedFrom":subQ2}),-1.0]])]});}
            var Q1;
            {var subQ8=sQuery(id+"F1.wireOp",EDGE,"E151.sketch_text.stroke-8");Q1=makeQuery(id+"F1.imprint","IMPRINT",FACE,{"disambiguationData":[TD([[makeQuery(id+"F1.imprint","IMPRINT",EDGE,{"derivedFrom":subQ8}),-1.0]])]});}
            var Q2;
            {var subQ9=sQuery(id+"F1.wireOp",EDGE,"E151.sketch_text.stroke-40");Q2=makeQuery(id+"F1.imprint","IMPRINT",FACE,{"disambiguationData":[TD([[makeQuery(id+"F1.imprint","IMPRINT",EDGE,{"derivedFrom":subQ9}),-1.0]])]});}
            var Q3;
            {var subQ2=sQuery(id+"F1.wireOp",EDGE,"E151.sketch_text.stroke-65");Q3=makeQuery(id+"F1.imprint","IMPRINT",FACE,{"disambiguationData":[TD([[makeQuery(id+"F1.imprint","IMPRINT",EDGE,{"derivedFrom":subQ2}),-1.0]])]});}
            var Q4;
            {var subQ13=sQuery(id+"F1.wireOp",EDGE,"E151.sketch_text.stroke-73");Q4=makeQuery(id+"F1.imprint","IMPRINT",FACE,{"disambiguationData":[TD([[makeQuery(id+"F1.imprint","IMPRINT",EDGE,{"derivedFrom":subQ13}),-1.0]])]});}
            var Q5;
            Q5=makeQuery(id+"F1.imprint","IMPRINT",FACE,{"disambiguationData":[TD([[makeQuery(id+"F1.imprint","IMPRINT",EDGE,{"derivedFrom":sQuery(id+"F1.wireOp",EDGE,"E151.sketch_text.stroke-89")}),-1.0]])]});
            var Q6;
            Q6=makeQuery(id+"F1.imprint","IMPRINT",FACE,{"disambiguationData":[TD([[makeQuery(id+"F1.imprint","IMPRINT",EDGE,{"derivedFrom":sQuery(id+"F1.wireOp",EDGE,"E151.sketch_text.stroke-98")}),-1.0]])]});
            var Q7;
            Q7=makeQuery(id+"F1.imprint","IMPRINT",FACE,{"disambiguationData":[TD([[makeQuery(id+"F1.imprint","IMPRINT",EDGE,{"derivedFrom":sQuery(id+"F1.wireOp",EDGE,"E151.sketch_text.stroke-107")}),-1.0]])]});
            var Q8;
            Q8=makeQuery(id+"F1.imprint","IMPRINT",FACE,{"disambiguationData":[TD([[makeQuery(id+"F1.imprint","IMPRINT",EDGE,{"derivedFrom":sQuery(id+"F1.wireOp",EDGE,"E151.sketch_text.stroke-116")}),-1.0]])]});
            var Q9;
            Q9=makeQuery(id+"F1.imprint","IMPRINT",FACE,{"disambiguationData":[TD([[makeQuery(id+"F1.imprint","IMPRINT",EDGE,{"derivedFrom":sQuery(id+"F1.wireOp",EDGE,"E151.sketch_text.stroke-136")}),-1.0]])]});
            var Q10;
            Q10=makeQuery(id+"F1.imprint","IMPRINT",FACE,{"disambiguationData":[TD([[makeQuery(id+"F1.imprint","IMPRINT",EDGE,{"derivedFrom":sQuery(id+"F1.wireOp",EDGE,"E151.sketch_text.stroke-145")}),-1.0]])]});
            var Q11;
            Q11=makeQuery(id+"F1.imprint","IMPRINT",FACE,{"disambiguationData":[TD([[makeQuery(id+"F1.imprint","IMPRINT",EDGE,{"derivedFrom":sQuery(id+"F1.wireOp",EDGE,"E151.sketch_text.stroke-165")}),-1.0]])]});
            var Q12;
            Q12=makeQuery(id+"F1.imprint","IMPRINT",FACE,{"disambiguationData":[TD([[makeQuery(id+"F1.imprint","IMPRINT",EDGE,{"derivedFrom":sQuery(id+"F1.wireOp",EDGE,"E151.sketch_text.stroke-193")}),-1.0]])]});
            var Q13;
            Q13=makeQuery(id+"F1.imprint","IMPRINT",FACE,{"disambiguationData":[TD([[makeQuery(id+"F1.imprint","IMPRINT",EDGE,{"derivedFrom":sQuery(id+"F1.wireOp",EDGE,"E151.sketch_text.stroke-210")}),-1.0]])]});
            var Q14;
            Q14=makeQuery(id+"F1.imprint","IMPRINT",FACE,{"disambiguationData":[TD([[makeQuery(id+"F1.imprint","IMPRINT",EDGE,{"derivedFrom":sQuery(id+"F1.wireOp",EDGE,"E151.sketch_text.stroke-229")}),-1.0]])]});
            var Q15;
            Q15=makeQuery(id+"F1.imprint","IMPRINT",FACE,{"disambiguationData":[TD([[makeQuery(id+"F1.imprint","IMPRINT",EDGE,{"derivedFrom":sQuery(id+"F1.wireOp",EDGE,"E151.sketch_text.stroke-254")}),-1.0]])]});
            extrude(context, id + "F5", {"entities" : qUnion([Q0, Q1, Q2, Q3, Q4, Q5, Q6, Q7, Q8, Q9, Q10, Q11, Q12, Q13, Q14, Q15]), "depth" : 12.7 * mm});
        }
        {
            var Q0;
            Q0=qCreatedBy(makeId("Top.planeOp"),FACE);
            var sketch = newSketch(context, id + "F6", { "sketchPlane" : qUnion([Q0])});
            skLineSegment(sketch, "E166.bottom", {"start": v(692.29, -120.65) * mm, "end": v(1301.89, -120.65) * mm});
            skLineSegment(sketch, "E166.top", {"start": v(692.29, -730.25) * mm, "end": v(1301.89, -730.25) * mm});
            skLineSegment(sketch, "E166.left", {"start": v(692.29, -120.65) * mm, "end": v(692.29, -730.25) * mm});
            skLineSegment(sketch, "E166.right", {"start": v(1301.89, -120.65) * mm, "end": v(1301.89, -730.25) * mm});
            skSolve(sketch);
        }
        {
            var Q0;
            Q0=makeQuery(id+"F6.imprint","IMPRINT",FACE,{"disambiguationData":[TD([[makeQuery(id+"F6.imprint","IMPRINT",EDGE,{"derivedFrom":sQuery(id+"F6.wireOp",EDGE,"E166.bottom")}),-1.0]])]});
            extrude(context, id + "F7", {"entities" : qUnion([Q0]), "oppositeDirection" : true, "depth" : 76.2 * mm});
        }
        {
            var Q0;
            Q0=makeQuery(id+"F1.imprint","IMPRINT",FACE,{"disambiguationData":[TD([[makeQuery(id+"F1.imprint","IMPRINT",EDGE,{"derivedFrom":sQuery(id+"F1.wireOp",EDGE,"E125.0")}),1.0]])]});
            var Q1;
            Q1=makeQuery(id+"F1.imprint","IMPRINT",FACE,{"disambiguationData":[TD([[makeQuery(id+"F1.imprint","IMPRINT",EDGE,{"derivedFrom":sQuery(id+"F1.wireOp",EDGE,"E125.0")}),-1.0]])]});
            var Q2;
            Q2=makeQuery(id+"F1.imprint","IMPRINT",FACE,{"disambiguationData":[TD([[makeQuery(id+"F1.imprint","IMPRINT",EDGE,{"derivedFrom":sQuery(id+"F1.wireOp",EDGE,"E126.0")}),-1.0]])]});
            var Q3;
            Q3=makeQuery(id+"F1.imprint","IMPRINT",FACE,{"disambiguationData":[TD([[makeQuery(id+"F1.imprint","IMPRINT",EDGE,{"derivedFrom":sQuery(id+"F1.wireOp",EDGE,"E127.0")}),-1.0]])]});
            var Q4;
            Q4=makeQuery(id+"F1.imprint","IMPRINT",FACE,{"disambiguationData":[TD([[makeQuery(id+"F1.imprint","IMPRINT",EDGE,{"derivedFrom":sQuery(id+"F1.wireOp",EDGE,"E128.0")}),-1.0]])]});
            var Q5;
            Q5=makeQuery(id+"F1.imprint","IMPRINT",FACE,{"disambiguationData":[TD([[makeQuery(id+"F1.imprint","IMPRINT",EDGE,{"derivedFrom":sQuery(id+"F1.wireOp",EDGE,"E129.0")}),-1.0]])]});
            var Q6;
            Q6=makeQuery(id+"F1.imprint","IMPRINT",FACE,{"disambiguationData":[TD([[makeQuery(id+"F1.imprint","IMPRINT",EDGE,{"derivedFrom":sQuery(id+"F1.wireOp",EDGE,"E130.0")}),-1.0]])]});
            var Q7;
            Q7=makeQuery(id+"F1.imprint","IMPRINT",FACE,{"disambiguationData":[TD([[makeQuery(id+"F1.imprint","IMPRINT",EDGE,{"derivedFrom":sQuery(id+"F1.wireOp",EDGE,"E131.0")}),-1.0]])]});
            var Q8;
            Q8=makeQuery(id+"F1.imprint","IMPRINT",FACE,{"disambiguationData":[TD([[makeQuery(id+"F1.imprint","IMPRINT",EDGE,{"derivedFrom":sQuery(id+"F1.wireOp",EDGE,"E132.0")}),-1.0]])]});
            var Q9;
            Q9=makeQuery(id+"F1.imprint","IMPRINT",FACE,{"disambiguationData":[TD([[makeQuery(id+"F1.imprint","IMPRINT",EDGE,{"derivedFrom":sQuery(id+"F1.wireOp",EDGE,"E133.0")}),-1.0]])]});
            var Q10;
            Q10=makeQuery(id+"F1.imprint","IMPRINT",FACE,{"disambiguationData":[TD([[makeQuery(id+"F1.imprint","IMPRINT",EDGE,{"derivedFrom":sQuery(id+"F1.wireOp",EDGE,"E134.0")}),-1.0]])]});
            var Q11;
            Q11=makeQuery(id+"F1.imprint","IMPRINT",FACE,{"disambiguationData":[TD([[makeQuery(id+"F1.imprint","IMPRINT",EDGE,{"derivedFrom":sQuery(id+"F1.wireOp",EDGE,"E135.0")}),-1.0]])]});
            var Q12;
            Q12=makeQuery(id+"F1.imprint","IMPRINT",FACE,{"disambiguationData":[TD([[makeQuery(id+"F1.imprint","IMPRINT",EDGE,{"derivedFrom":sQuery(id+"F1.wireOp",EDGE,"E136.0")}),-1.0]])]});
            var Q13;
            Q13=makeQuery(id+"F1.imprint","IMPRINT",FACE,{"disambiguationData":[TD([[makeQuery(id+"F1.imprint","IMPRINT",EDGE,{"derivedFrom":sQuery(id+"F1.wireOp",EDGE,"E137.0")}),-1.0]])]});
            extrude(context, id + "F8", {"entities" : qUnion([Q0, Q1, Q2, Q3, Q4, Q5, Q6, Q7, Q8, Q9, Q10, Q11, Q12, Q13]), "oppositeDirection" : true, "depth" : 152.4 * mm, "hasSecondDirection" : true, "secondDirectionOppositeDirection" : true, "secondDirectionDepth" : 50.9 * mm});
        }
    });
